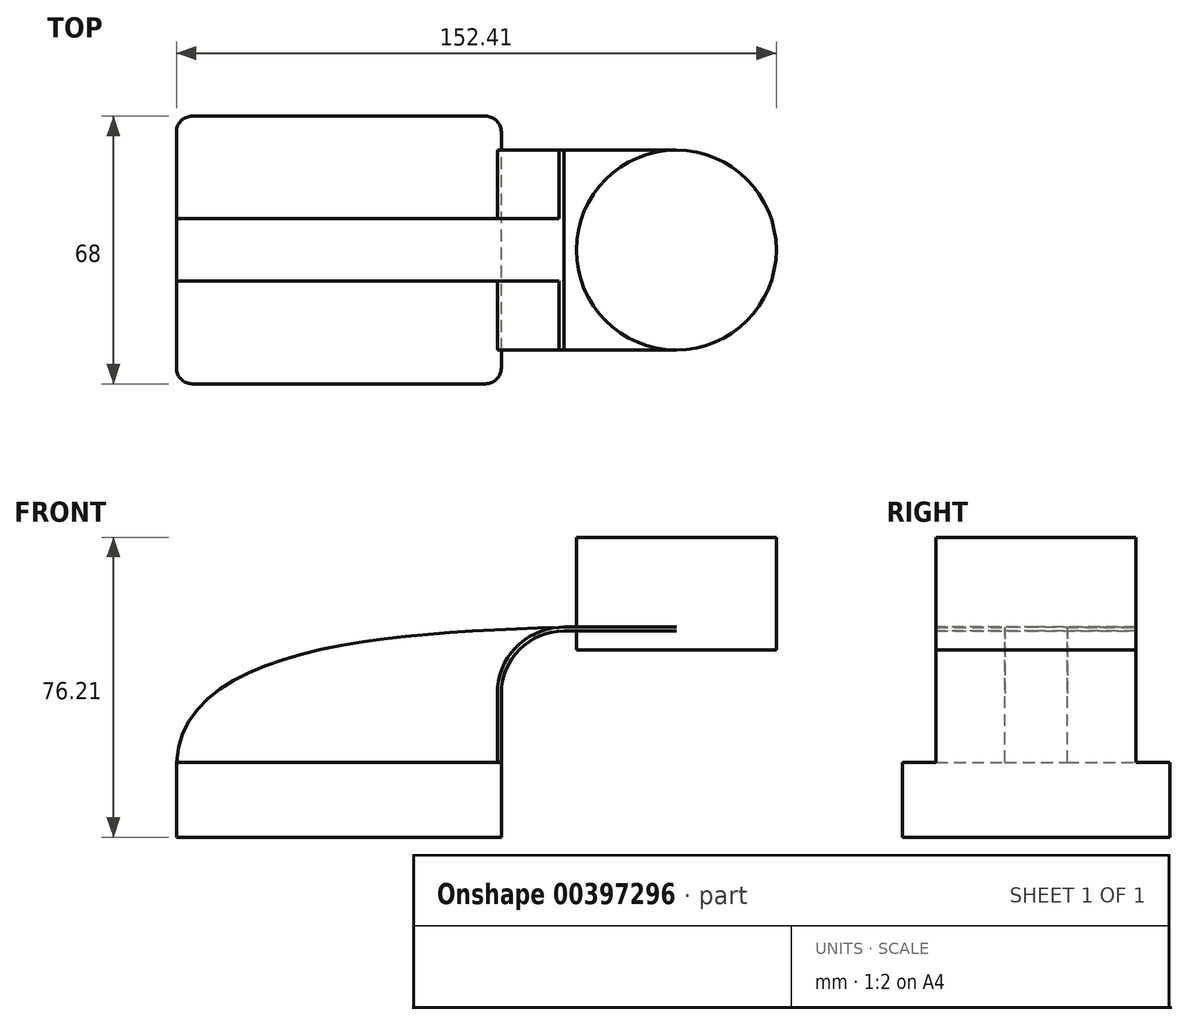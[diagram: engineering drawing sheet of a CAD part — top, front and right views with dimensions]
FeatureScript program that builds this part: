
annotation { "Feature Type Name" : "Feature", "Feature Type Description" : "" }
export const myFeature = defineFeature(function(context is Context, id is Id, definition is map)
    precondition{}
    {
        {
            var Q0;
            Q0=qCreatedBy(makeId("Front.planeOp"),FACE);
            var sketch = newSketch(context, id + "F0", { "sketchPlane" : qUnion([Q0])});
            skLineSegment(sketch, "E0.rect.bottom", {"start": v(-41.28, 9.52) * mm, "end": v(41.28, 9.52) * mm});
            skLineSegment(sketch, "E0.rect.top", {"start": v(-41.28, -9.52) * mm, "end": v(41.28, -9.52) * mm});
            skLineSegment(sketch, "E0.rect.left", {"start": v(-41.28, 9.52) * mm, "end": v(-41.28, -9.52) * mm});
            skLineSegment(sketch, "E0.rect.right", {"start": v(41.28, 9.52) * mm, "end": v(41.28, -9.52) * mm});
            skPoint(sketch, "E0.rect.middle", {"position": v(0, 0) * mm});
            skLineSegment(sketch, "E1", {"start": v(41.28, 9.52) * mm, "end": v(41.28, 27) * mm});
            skArc(sketch, "E2", {"start": v(41.28, 27) * mm, "mid": v(45.92, 38.23) * mm, "end": v(57.15, 42.88) * mm});
            skLineSegment(sketch, "E3", {"start": v(57.15, 42.88) * mm, "end": v(85.72, 42.88) * mm});
            skLineSegment(sketch, "E4.rect.bottom", {"start": v(60.32, 38.1) * mm, "end": v(111.12, 38.1) * mm});
            skLineSegment(sketch, "E4.rect.top", {"start": v(60.32, 66.68) * mm, "end": v(111.12, 66.68) * mm});
            skLineSegment(sketch, "E4.rect.left", {"start": v(60.32, 38.1) * mm, "end": v(60.32, 66.68) * mm});
            skLineSegment(sketch, "E4.rect.right", {"start": v(111.13, 38.1) * mm, "end": v(111.12, 66.68) * mm});
            skPoint(sketch, "E4.rect.middle", {"position": v(85.72, 52.39) * mm});
            skLineSegment(sketch, "E5.0", {"start": v(57.15, 43.88) * mm, "end": v(85.72, 43.88) * mm});
            skArc(sketch, "E5.1", {"start": v(40.28, 27) * mm, "mid": v(45.22, 38.93) * mm, "end": v(57.15, 43.88) * mm});
            skLineSegment(sketch, "E5.2", {"start": v(40.27, 9.52) * mm, "end": v(40.27, 27) * mm});
            skLineSegment(sketch, "E6", {"start": v(85.72, 38.1) * mm, "end": v(85.72, 66.68) * mm});
            skFitSpline(sketch, "E7", {"points": [v(-41.28, 9.53) * mm, v(57.15, 43.88) * mm], "startDerivative": vector(5.2, 92.34) * mm, "endDerivative": vector(120.92, 4.22) * mm});
            skSolve(sketch);
        }
        {
            var Q0;
            Q0=makeQuery(id+"F0.imprint","IMPRINT",FACE,{"disambiguationData":[TD([[makeQuery(id+"F0.imprint","IMPRINT",EDGE,{"derivedFrom":sQuery(id+"F0.wireOp",EDGE,"E0.rect.top")}),1.0]])]});
            extrude(context, id + "F1", {"entities" : qUnion([Q0]), "endBound" : BoundingType.SYMMETRIC, "depth" : 68 * mm});
        }
        {
            var Q0;
            {var subQ9=sQuery(id+"F0.wireOp",EDGE,"E1");Q0=makeQuery(id+"F0.imprint","IMPRINT",FACE,{"disambiguationData":[TD([[makeQuery(id+"F0.imprint","IMPRINT",EDGE,{"derivedFrom":subQ9}),1.0]])]});}
            var Q1;
            {var subQ0=sQuery(id+"F0.wireOp",EDGE,"E6");var subQ1=sQuery(id+"F0.wireOp",EDGE,"E3");var subQ2=makeQuery(id+"F0.imprint","INTERSECT",VERTEX,{"derivedFrom":[subQ1,subQ0]});Q1=makeQuery(id+"F0.imprint","IMPRINT",FACE,{"disambiguationData":[TD([[makeQuery(id+"F0.imprint","IMPRINT",EDGE,{"disambiguationData":[TD([[subQ2,1.0]])],"derivedFrom":subQ1}),1.0]])]});}
            extrude(context, id + "F2", {"entities" : qUnion([Q0, Q1]), "operationType" : NewBodyOperationType.ADD, "endBound" : BoundingType.SYMMETRIC, "depth" : 50.8 * mm});
        }
        {
            var Q0;
            {var subQ3=sQuery(id+"F0.wireOp",EDGE,"E5.2");Q0=makeQuery(id+"F0.imprint","IMPRINT",FACE,{"disambiguationData":[TD([[makeQuery(id+"F0.imprint","IMPRINT",EDGE,{"derivedFrom":subQ3}),1.0]])]});}
            extrude(context, id + "F3", {"entities" : qUnion([Q0]), "operationType" : NewBodyOperationType.ADD, "endBound" : BoundingType.SYMMETRIC, "depth" : 15.88 * mm});
        }
        {
            var Q0;
            {var subQ5=sQuery(id+"F0.wireOp",EDGE,"E4.rect.right");Q0=makeQuery(id+"F0.imprint","IMPRINT",FACE,{"disambiguationData":[TD([[makeQuery(id+"F0.imprint","IMPRINT",EDGE,{"derivedFrom":subQ5}),1.0]])]});}
            var Q1;
            Q1=sQuery(id+"F0.wireOp",EDGE,"E6");
            revolve(context, id + "F4", {"operationType" : NewBodyOperationType.ADD, "entities" : qUnion([Q0]), "axis" : qUnion([Q1]), "revolveType" : RevolveType.FULL});
        }
        {
            var Q0;
            Q0=makeQuery(id+"F1.opExtrude","CAP_EDGE",EDGE,{"disambiguationData":[OSD([sQuery(id+"F0.wireOp",EDGE,"E0.rect.right")])],"isStart":false});
            var Q1;
            Q1=makeQuery(id+"F1.opExtrude","CAP_EDGE",EDGE,{"disambiguationData":[OSD([sQuery(id+"F0.wireOp",EDGE,"E0.rect.left")])],"isStart":false});
            var Q2;
            Q2=makeQuery(id+"F1.opExtrude","CAP_EDGE",EDGE,{"disambiguationData":[OSD([sQuery(id+"F0.wireOp",EDGE,"E0.rect.right")])],"isStart":true});
            var Q3;
            Q3=makeQuery(id+"F1.opExtrude","CAP_EDGE",EDGE,{"disambiguationData":[OSD([sQuery(id+"F0.wireOp",EDGE,"E0.rect.left")])],"isStart":true});
            fillet(context, id + "F5", {"entities" : qUnion([Q0, Q1, Q2, Q3]), "radius" : 4 * mm, "tangentPropagation" : true, "allowEdgeOverflow" : false});
        }
        {
            var Q0;
            Q0=makeQuery(id+"F4.opRevolve","SWEPT_FACE",FACE,{"disambiguationData":[OSD([sQuery(id+"F0.wireOp",EDGE,"E4.rect.top")])]});
            extrude(context, id + "F6", {"entities" : qUnion([Q0]), "operationType" : NewBodyOperationType.ADD, "oppositeDirection" : true, "depth" : 16 * mm});
        }
    });
